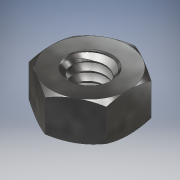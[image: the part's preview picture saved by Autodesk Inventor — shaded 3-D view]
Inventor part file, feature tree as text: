
AUTODESK INVENTOR PART (.ipt)
format: ipt  version: 2017 (Build 210142000, 142)  size: 354,816 bytes
history: native  units: mm
features: other x1, mirror x1
ambient origin geometry x8: Origin, YZ Plane, XZ Plane, XY Plane, X Axis, Y Axis, Z Axis, Center Point
bodies: Body1 (feature_tree)
feature tree (2):
  other  "Sólido1"
  mirror  "Mirror1"
